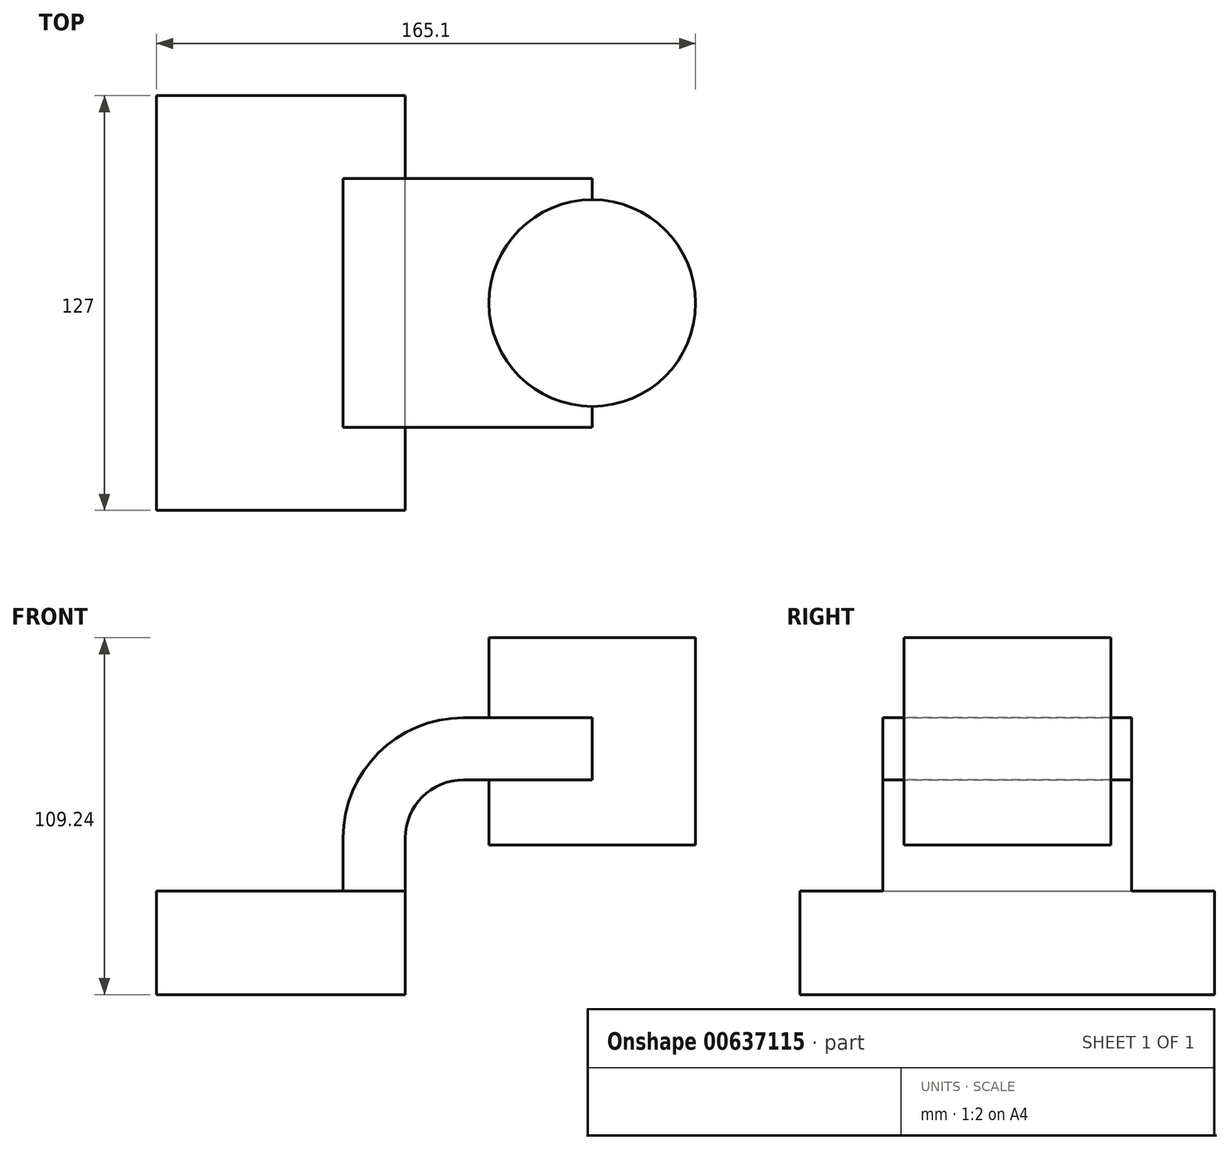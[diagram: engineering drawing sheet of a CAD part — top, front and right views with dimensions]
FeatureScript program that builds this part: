
annotation { "Feature Type Name" : "Feature", "Feature Type Description" : "" }
export const myFeature = defineFeature(function(context is Context, id is Id, definition is map)
    precondition{}
    {
        {
            var Q0;
            Q0=qCreatedBy(makeId("Front.planeOp"),FACE);
            var sketch = newSketch(context, id + "F0", { "sketchPlane" : qUnion([Q0])});
            skLineSegment(sketch, "E0.bottom", {"start": v(-38.1, 15.87) * mm, "end": v(38.1, 15.88) * mm});
            skLineSegment(sketch, "E0.top", {"start": v(-38.1, -15.88) * mm, "end": v(38.1, -15.88) * mm});
            skLineSegment(sketch, "E0.left", {"start": v(-38.1, 15.87) * mm, "end": v(-38.1, -15.88) * mm});
            skLineSegment(sketch, "E0.right", {"start": v(38.1, 15.88) * mm, "end": v(38.1, -15.87) * mm});
            skPoint(sketch, "E0.middle", {"position": v(0, 0) * mm});
            skLineSegment(sketch, "E1.bottom", {"start": v(127, 93.36) * mm, "end": v(76.2, 93.36) * mm});
            skLineSegment(sketch, "E1.top", {"start": v(127, 29.86) * mm, "end": v(76.2, 29.86) * mm});
            skLineSegment(sketch, "E1.left", {"start": v(127, 93.36) * mm, "end": v(127, 29.86) * mm});
            skLineSegment(sketch, "E1.right", {"start": v(76.2, 93.36) * mm, "end": v(76.2, 29.86) * mm});
            skPoint(sketch, "E1.middle", {"position": v(101.6, 61.61) * mm});
            skLineSegment(sketch, "E2", {"start": v(38.1, 15.88) * mm, "end": v(38.1, 32.06) * mm});
            skArc(sketch, "E3", {"start": v(38.1, 32.06) * mm, "mid": v(43.3, 44.63) * mm, "end": v(55.88, 49.84) * mm});
            skLineSegment(sketch, "E4", {"start": v(55.88, 49.84) * mm, "end": v(95.35, 49.84) * mm});
            skLineSegment(sketch, "E5.0", {"start": v(55.88, 68.89) * mm, "end": v(95.35, 68.89) * mm});
            skArc(sketch, "E5.1", {"start": v(19.05, 32.06) * mm, "mid": v(29.84, 58.1) * mm, "end": v(55.88, 68.89) * mm});
            skLineSegment(sketch, "E5.2", {"start": v(19.05, 15.88) * mm, "end": v(19.05, 32.06) * mm});
            skLineSegment(sketch, "E6", {"start": v(95.35, 29.86) * mm, "end": v(95.35, 93.36) * mm});
            skFitSpline(sketch, "E7", {"points": [v(-38.1, 15.87) * mm, v(55.88, 68.89) * mm], "startDerivative": vector(3.66, 84.22) * mm, "endDerivative": vector(124.05, -2.81) * mm});
            skSolve(sketch);
        }
        {
            var Q0;
            Q0=makeQuery(id+"F0.imprint","IMPRINT",FACE,{"disambiguationData":[TD([[makeQuery(id+"F0.imprint","IMPRINT",EDGE,{"derivedFrom":sQuery(id+"F0.wireOp",EDGE,"E0.top")}),1.0]])]});
            extrude(context, id + "F1", {"entities" : qUnion([Q0]), "endBound" : BoundingType.SYMMETRIC, "depth" : 127 * mm, "offsetDistance" : 25.4 * mm});
        }
        {
            var Q0;
            {var subQ1=sQuery(id+"F0.wireOp",EDGE,"E2");Q0=makeQuery(id+"F0.imprint","IMPRINT",FACE,{"disambiguationData":[TD([[makeQuery(id+"F0.imprint","IMPRINT",EDGE,{"derivedFrom":subQ1}),1.0]])]});}
            var Q1;
            {var subQ0=sQuery(id+"F0.wireOp",EDGE,"E5.0");var subQ1=sQuery(id+"F0.wireOp",EDGE,"E1.right");var subQ2=makeQuery(id+"F0.imprint","INTERSECT",VERTEX,{"derivedFrom":[subQ1,subQ0]});Q1=makeQuery(id+"F0.imprint","IMPRINT",FACE,{"disambiguationData":[TD([[makeQuery(id+"F0.imprint","IMPRINT",EDGE,{"disambiguationData":[TD([[subQ2,-1.0]])],"derivedFrom":subQ1}),1.0]])]});}
            extrude(context, id + "F2", {"entities" : qUnion([Q0, Q1]), "operationType" : NewBodyOperationType.ADD, "endBound" : BoundingType.SYMMETRIC, "depth" : 76.2 * mm, "offsetDistance" : 25.4 * mm});
        }
        {
            var Q0;
            Q0=makeQuery(id+"F0.imprint","IMPRINT",FACE,{"disambiguationData":[TD([[makeQuery(id+"F0.imprint","IMPRINT",EDGE,{"derivedFrom":sQuery(id+"F0.wireOp",EDGE,"E5.1")}),1.0]])]});
            extrude(context, id + "F3", {"entities" : qUnion([Q0]), "operationType" : NewBodyOperationType.ADD, "endBound" : BoundingType.SYMMETRIC, "depth" : 25.4 * mm, "offsetDistance" : 25.4 * mm});
        }
        {
            var Q0;
            {var subQ4=sQuery(id+"F0.wireOp",EDGE,"E1.left");Q0=makeQuery(id+"F0.imprint","IMPRINT",FACE,{"disambiguationData":[TD([[makeQuery(id+"F0.imprint","IMPRINT",EDGE,{"derivedFrom":subQ4}),-1.0]])]});}
            var Q1;
            Q1=sQuery(id+"F0.wireOp",EDGE,"E6");
            revolve(context, id + "F4", {"operationType" : NewBodyOperationType.ADD, "entities" : qUnion([Q0]), "axis" : qUnion([Q1]), "revolveType" : RevolveType.FULL});
        }
    });
